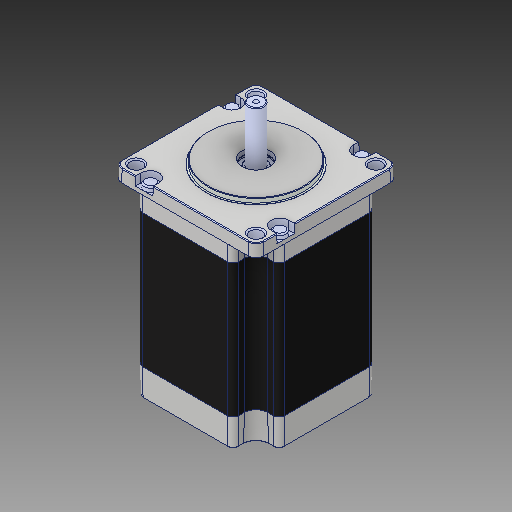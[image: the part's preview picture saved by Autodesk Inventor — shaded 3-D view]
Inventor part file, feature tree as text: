
AUTODESK INVENTOR PART (.ipt)
format: ipt  version: 2018 (Build 220112000, 112)  size: 454,656 bytes
history: native  units: mm
features: other x6, sketch x1
ambient origin geometry x8: Origin, YZ Plane, XZ Plane, XY Plane, X Axis, Y Axis, Z Axis, Center Point
bodies: Body1 (feature_tree), Body2 (feature_tree)
feature tree (7):
  other  "stepper motor NEMA 23 57x76.ipt"
  other  "Фаска2::stepper motor NEMA 23 57x76.ipt"
  other  "Вырез-Вытянуть12::stepper motor NEMA 23 57x76.ipt"
  other  "OperaçãoIdentificador1"
  sketch  "Sketch1"  dims[d0=10.0mm]
  other  "Sólido1"
  other  "Sólido2"
